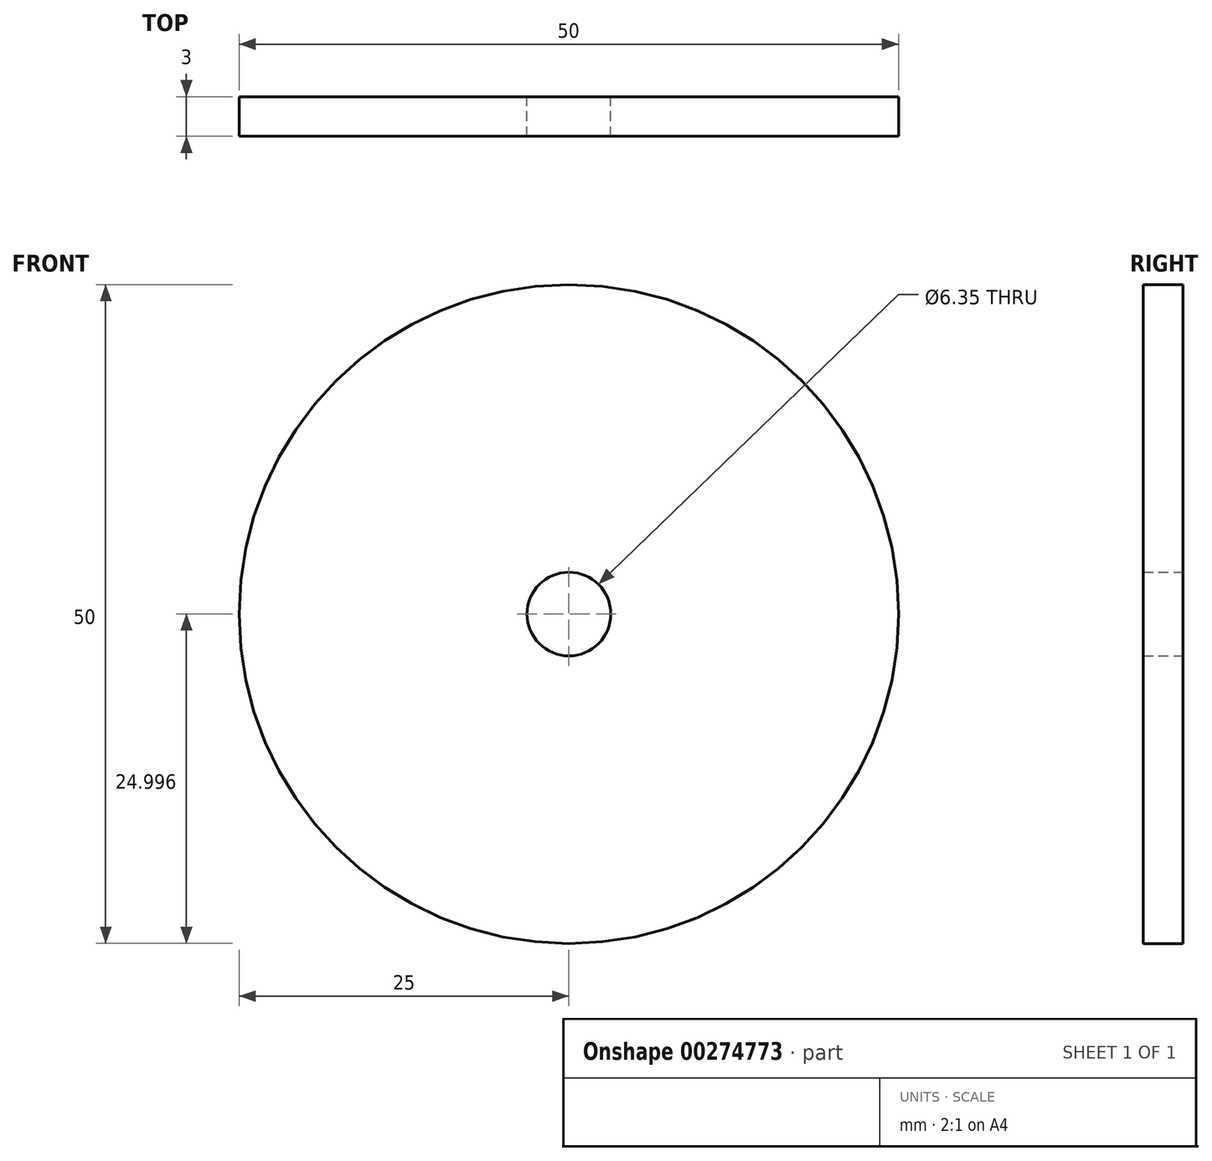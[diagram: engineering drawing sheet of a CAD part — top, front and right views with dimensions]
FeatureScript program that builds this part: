
annotation { "Feature Type Name" : "Feature", "Feature Type Description" : "" }
export const myFeature = defineFeature(function(context is Context, id is Id, definition is map)
    precondition{}
    {
        {
            var Q0;
            Q0=qCreatedBy(makeId("Front.planeOp"),FACE);
            var sketch = newSketch(context, id + "F0", { "sketchPlane" : qUnion([Q0])});
            skCircle(sketch, "E0", {"center": v(0, 1.5) * mm, "radius": 3.17 * mm});
            skCircle(sketch, "E1", {"center": v(0, 1.5) * mm, "radius": 25 * mm});
            skSolve(sketch);
        }
        {
            var Q0;
            Q0=makeQuery(id+"F0.imprint","IMPRINT",FACE,{"disambiguationData":[TD([[makeQuery(id+"F0.imprint","IMPRINT",EDGE,{"derivedFrom":sQuery(id+"F0.wireOp",EDGE,"E0")}),-1.0]])]});
            extrude(context, id + "F1", {"entities" : qUnion([Q0]), "depth" : 3 * mm});
        }
    });
